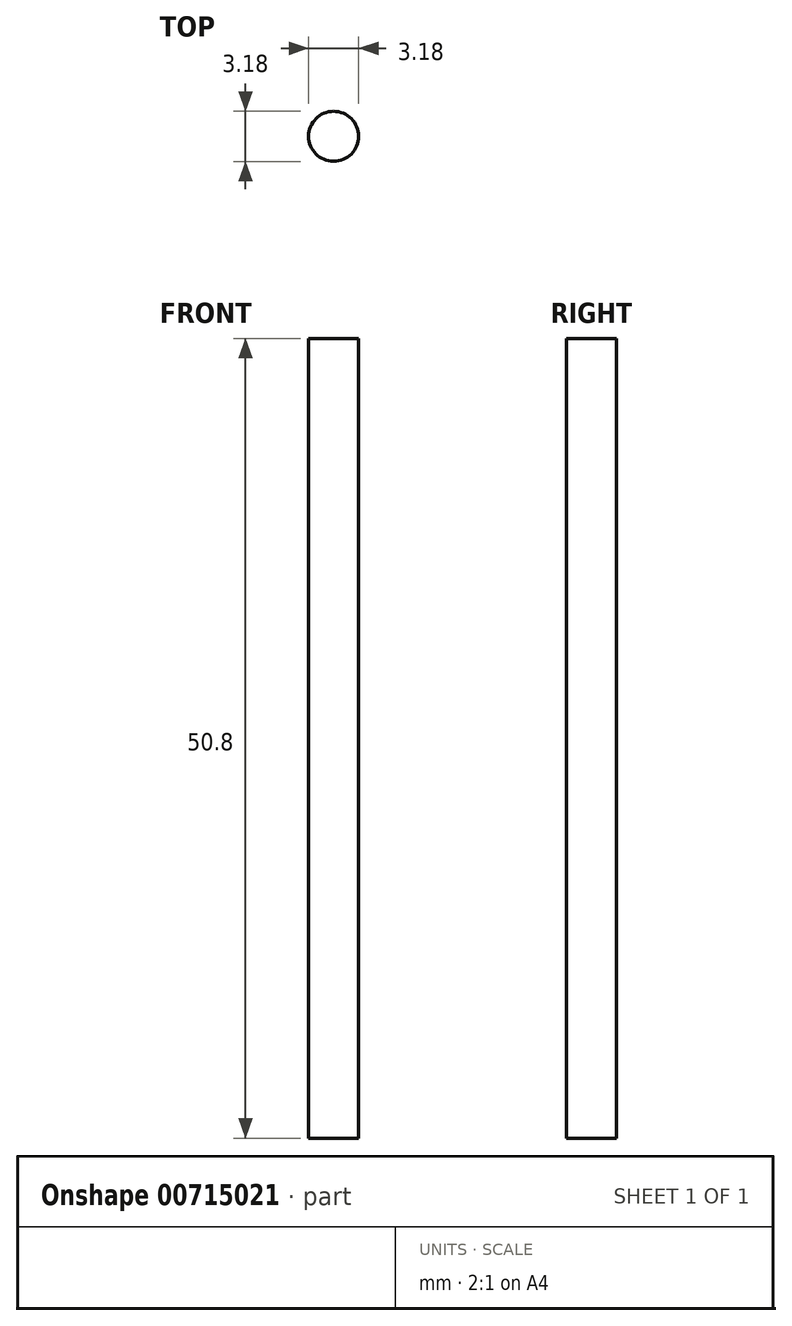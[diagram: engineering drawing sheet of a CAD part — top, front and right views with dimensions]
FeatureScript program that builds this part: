
annotation { "Feature Type Name" : "Feature", "Feature Type Description" : "" }
export const myFeature = defineFeature(function(context is Context, id is Id, definition is map)
    precondition{}
    {
        {
            var Q0;
            Q0=qCreatedBy(makeId("Top.planeOp"),FACE);
            var sketch = newSketch(context, id + "F0", { "sketchPlane" : qUnion([Q0])});
            skCircle(sketch, "E0", {"center": v(0, 0) * mm, "radius": 1.59 * mm});
            skSolve(sketch);
        }
        {
            var Q0;
            Q0 = qSketchRegion(id + "F0", true);
            extrude(context, id + "F1", {"entities" : qUnion([Q0]), "depth" : 50.8 * mm, "offsetDistance" : 25.4 * mm});
        }
    });
